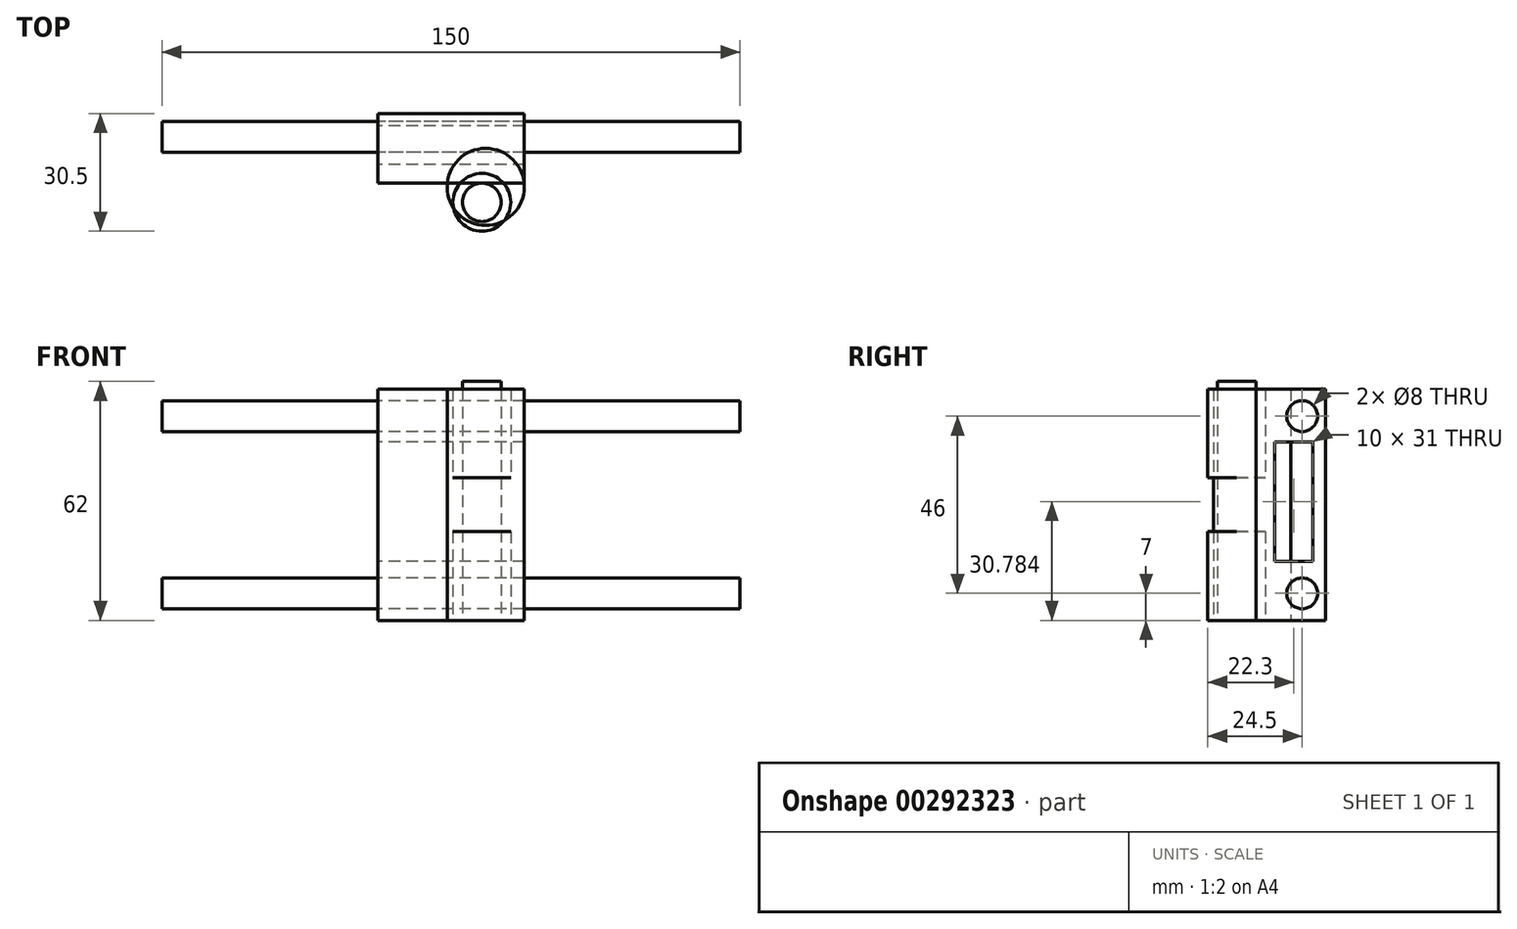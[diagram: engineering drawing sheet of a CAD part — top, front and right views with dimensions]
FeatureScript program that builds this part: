
annotation { "Feature Type Name" : "Feature", "Feature Type Description" : "" }
export const myFeature = defineFeature(function(context is Context, id is Id, definition is map)
    precondition{}
    {
        {
            var Q0;
            Q0=qCreatedBy(makeId("Top.planeOp"),FACE);
            var sketch = newSketch(context, id + "F0", { "sketchPlane" : qUnion([Q0])});
            skLineSegment(sketch, "E0.bottom", {"start": v(19, -9) * mm, "end": v(-19, -9) * mm});
            skLineSegment(sketch, "E0.top", {"start": v(19, 9) * mm, "end": v(-19, 9) * mm});
            skLineSegment(sketch, "E0.left", {"start": v(19, -9) * mm, "end": v(19, 9) * mm});
            skLineSegment(sketch, "E0.right", {"start": v(-19, -9) * mm, "end": v(-19, 9) * mm});
            skPoint(sketch, "E0.middle", {"position": v(0, 0) * mm});
            skSolve(sketch);
        }
        {
            var Q0;
            Q0 = qSketchRegion(id + "F0", true);
            extrude(context, id + "F1", {"entities" : qUnion([Q0]), "depth" : 60 * mm});
        }
        {
            var Q0;
            Q0=qCreatedBy(makeId("Right.planeOp"),FACE);
            var sketch = newSketch(context, id + "F2", { "sketchPlane" : qUnion([Q0])});
            skCircle(sketch, "E1", {"center": v(0, 0) * mm, "radius": 4 * mm});
            skSolve(sketch);
        }
        {
            var Q0;
            Q0 = qSketchRegion(id + "F2", true);
            extrude(context, id + "F3", {"entities" : qUnion([Q0]), "endBound" : BoundingType.SYMMETRIC, "depth" : 150 * mm});
        }
        {
            var Q0;
            Q0=makeQuery(id+"F3.opExtrude","SWEPT_BODY",BODY,{"disambiguationData":[OSD([sQuery(id+"F2.wireOp",EDGE,"E1")])]});
            transform(context, id + "F4", {"entities" : qUnion([Q0]), "transformType" : TransformType.TRANSLATION_3D, "dx" : 0 * mm, "dy" : 3 * mm, "dz" : 7 * mm, "makeCopy" : false});
        }
        {
            var Q0;
            Q0=makeQuery(id+"F3.opExtrude","SWEPT_BODY",BODY,{"disambiguationData":[OSD([sQuery(id+"F2.wireOp",EDGE,"E1")])]});
            transform(context, id + "F5", {"entities" : qUnion([Q0]), "transformType" : TransformType.COPY});
        }
        {
            var Q0;
            Q0=makeQuery(id+"F5.opPattern","COPY",BODY,{"derivedFrom":makeQuery(id+"F3.opExtrude","SWEPT_BODY",BODY,{"disambiguationData":[OSD([sQuery(id+"F2.wireOp",EDGE,"E1")])]}),"instanceName":"1"});
            transform(context, id + "F6", {"entities" : qUnion([Q0]), "transformType" : TransformType.TRANSLATION_3D, "dx" : 0 * mm, "dy" : 0 * mm, "dz" : 46 * mm, "makeCopy" : false});
        }
        {
            var Q0;
            Q0=makeQuery(id+"F3.opExtrude","SWEPT_BODY",BODY,{"disambiguationData":[OSD([sQuery(id+"F2.wireOp",EDGE,"E1")])]});
            var Q1;
            Q1=makeQuery(id+"F5.opPattern","COPY",BODY,{"derivedFrom":makeQuery(id+"F3.opExtrude","SWEPT_BODY",BODY,{"disambiguationData":[OSD([sQuery(id+"F2.wireOp",EDGE,"E1")])]}),"instanceName":"1"});
            transform(context, id + "F7", {"entities" : qUnion([Q0, Q1]), "transformType" : TransformType.COPY});
        }
        {
            var Q0;
            Q0=makeQuery(id+"F7.opPattern","COPY",BODY,{"derivedFrom":makeQuery(id+"F3.opExtrude","SWEPT_BODY",BODY,{"disambiguationData":[OSD([sQuery(id+"F2.wireOp",EDGE,"E1")])]}),"instanceName":"1"});
            var Q1;
            Q1=makeQuery(id+"F7.opPattern","COPY",BODY,{"derivedFrom":makeQuery(id+"F5.opPattern","COPY",BODY,{"derivedFrom":makeQuery(id+"F3.opExtrude","SWEPT_BODY",BODY,{"disambiguationData":[OSD([sQuery(id+"F2.wireOp",EDGE,"E1")])]}),"instanceName":"1"}),"instanceName":"1"});
            var Q2;
            Q2=makeQuery(id+"F1.opExtrude","SWEPT_BODY",BODY,{"disambiguationData":[OSD([sQuery(id+"F0.wireOp",EDGE,"E0.bottom"),sQuery(id+"F0.wireOp",EDGE,"E0.top"),sQuery(id+"F0.wireOp",EDGE,"E0.left"),sQuery(id+"F0.wireOp",EDGE,"E0.right")])]});
            booleanBodies(context, id + "F8", {"operationType" : BooleanOperationType.SUBTRACTION, "tools" : qUnion([Q0, Q1]), "targets" : qUnion([Q2])});
        }
        {
            var Q0;
            Q0=qCreatedBy(makeId("Right.planeOp"),FACE);
            var sketch = newSketch(context, id + "F9", { "sketchPlane" : qUnion([Q0])});
            skLineSegment(sketch, "E2", {"start": v(5.8, 0) * mm, "end": v(9, 0) * mm});
            skLineSegment(sketch, "E3", {"start": v(9, 0) * mm, "end": v(5.8, 0) * mm});
            skLineSegment(sketch, "E4", {"start": v(5.8, 15.28) * mm, "end": v(5.8, 46.28) * mm});
            skLineSegment(sketch, "E5", {"start": v(5.8, 15.28) * mm, "end": v(-4.2, 15.28) * mm});
            skLineSegment(sketch, "E6", {"start": v(-4.2, 15.28) * mm, "end": v(-4.2, 46.28) * mm});
            skLineSegment(sketch, "E7", {"start": v(-4.2, 46.28) * mm, "end": v(5.8, 46.28) * mm});
            skSolve(sketch);
        }
        {
            var Q0;
            Q0 = qSketchRegion(id + "F9", true);
            extrude(context, id + "F10", {"entities" : qUnion([Q0]), "endBound" : BoundingType.SYMMETRIC, "depth" : 50 * mm});
        }
        {
            var Q0;
            Q0=makeQuery(id+"F10.opExtrude","SWEPT_BODY",BODY,{"disambiguationData":[OSD([sQuery(id+"F9.wireOp",EDGE,"E4"),sQuery(id+"F9.wireOp",EDGE,"E5"),sQuery(id+"F9.wireOp",EDGE,"E6"),sQuery(id+"F9.wireOp",EDGE,"E7")])]});
            var Q1;
            Q1=makeQuery(id+"F1.opExtrude","SWEPT_BODY",BODY,{"disambiguationData":[OSD([sQuery(id+"F0.wireOp",EDGE,"E0.bottom"),sQuery(id+"F0.wireOp",EDGE,"E0.top"),sQuery(id+"F0.wireOp",EDGE,"E0.left"),sQuery(id+"F0.wireOp",EDGE,"E0.right")])]});
            booleanBodies(context, id + "F11", {"operationType" : BooleanOperationType.SUBTRACTION, "tools" : qUnion([Q0]), "targets" : qUnion([Q1])});
        }
        {
            var Q0;
            Q0=qCreatedBy(makeId("Top.planeOp"),FACE);
            var sketch = newSketch(context, id + "F12", { "sketchPlane" : qUnion([Q0])});
            skCircle(sketch, "E8", {"center": v(0, 0) * mm, "radius": 7.5 * mm});
            skSolve(sketch);
        }
        {
            var Q0;
            Q0 = qSketchRegion(id + "F12", true);
            extrude(context, id + "F13", {"entities" : qUnion([Q0]), "depth" : 23 * mm});
        }
        {
            var Q0;
            Q0=makeQuery(id+"F13.opExtrude","SWEPT_BODY",BODY,{"disambiguationData":[OSD([sQuery(id+"F12.wireOp",EDGE,"E8")])]});
            transform(context, id + "F14", {"entities" : qUnion([Q0]), "transformType" : TransformType.TRANSLATION_3D, "dx" : 8 * mm, "dy" : -16 * mm, "dz" : 0 * mm, "makeCopy" : false});
        }
        {
            var Q0;
            Q0=makeQuery(id+"F13.opExtrude","SWEPT_BODY",BODY,{"disambiguationData":[OSD([sQuery(id+"F12.wireOp",EDGE,"E8")])]});
            transform(context, id + "F15", {"entities" : qUnion([Q0]), "transformType" : TransformType.TRANSLATION_3D, "dx" : 0 * mm, "dy" : 2 * mm, "dz" : 0 * mm, "makeCopy" : false});
        }
        {
            var Q0;
            Q0=makeQuery(id+"F13.opExtrude","SWEPT_BODY",BODY,{"disambiguationData":[OSD([sQuery(id+"F12.wireOp",EDGE,"E8")])]});
            transform(context, id + "F16", {"entities" : qUnion([Q0]), "transformType" : TransformType.COPY});
        }
        {
            var Q0;
            Q0=makeQuery(id+"F16.opPattern","COPY",BODY,{"derivedFrom":makeQuery(id+"F13.opExtrude","SWEPT_BODY",BODY,{"disambiguationData":[OSD([sQuery(id+"F12.wireOp",EDGE,"E8")])]}),"instanceName":"1"});
            transform(context, id + "F17", {"entities" : qUnion([Q0]), "transformType" : TransformType.TRANSLATION_3D, "dx" : 0 * mm, "dy" : 0 * mm, "dz" : 37 * mm, "makeCopy" : false});
        }
        {
            var Q0;
            Q0=qCreatedBy(makeId("Top.planeOp"),FACE);
            var sketch = newSketch(context, id + "F18", { "sketchPlane" : qUnion([Q0])});
            skCircle(sketch, "E9", {"center": v(0, 0) * mm, "radius": 5 * mm});
            skSolve(sketch);
        }
        {
            var Q0;
            Q0 = qSketchRegion(id + "F18", true);
            extrude(context, id + "F19", {"entities" : qUnion([Q0]), "depth" : 62 * mm});
        }
        {
            var Q0;
            Q0=makeQuery(id+"F19.opExtrude","SWEPT_BODY",BODY,{"disambiguationData":[OSD([sQuery(id+"F18.wireOp",EDGE,"E9")])]});
            transform(context, id + "F20", {"entities" : qUnion([Q0]), "transformType" : TransformType.TRANSLATION_3D, "dx" : 8 * mm, "dy" : -14 * mm, "dz" : 0 * mm, "makeCopy" : false});
        }
        {
            var Q0;
            Q0=makeQuery(id+"F13.opExtrude","SWEPT_BODY",BODY,{"disambiguationData":[OSD([sQuery(id+"F12.wireOp",EDGE,"E8")])]});
            var Q1;
            Q1=makeQuery(id+"F16.opPattern","COPY",BODY,{"derivedFrom":makeQuery(id+"F13.opExtrude","SWEPT_BODY",BODY,{"disambiguationData":[OSD([sQuery(id+"F12.wireOp",EDGE,"E8")])]}),"instanceName":"1"});
            var Q2;
            Q2=makeQuery(id+"F19.opExtrude","SWEPT_BODY",BODY,{"disambiguationData":[OSD([sQuery(id+"F18.wireOp",EDGE,"E9")])]});
            transform(context, id + "F21", {"entities" : qUnion([Q0, Q1, Q2]), "transformType" : TransformType.COPY});
        }
        {
            var Q0;
            Q0=qCreatedBy(makeId("Top.planeOp"),FACE);
            var sketch = newSketch(context, id + "F22", { "sketchPlane" : qUnion([Q0])});
            skCircle(sketch, "E10", {"center": v(0, 0) * mm, "radius": 10 * mm});
            skSolve(sketch);
        }
        {
            var Q0;
            Q0 = qSketchRegion(id + "F22", true);
            extrude(context, id + "F23", {"entities" : qUnion([Q0]), "depth" : 60 * mm});
        }
        {
            var Q0;
            Q0=makeQuery(id+"F23.opExtrude","SWEPT_BODY",BODY,{"disambiguationData":[OSD([sQuery(id+"F22.wireOp",EDGE,"E10")])]});
            transform(context, id + "F24", {"entities" : qUnion([Q0]), "transformType" : TransformType.TRANSLATION_3D, "dx" : 9 * mm, "dy" : -10 * mm, "dz" : 0 * mm, "makeCopy" : false});
        }
    });
